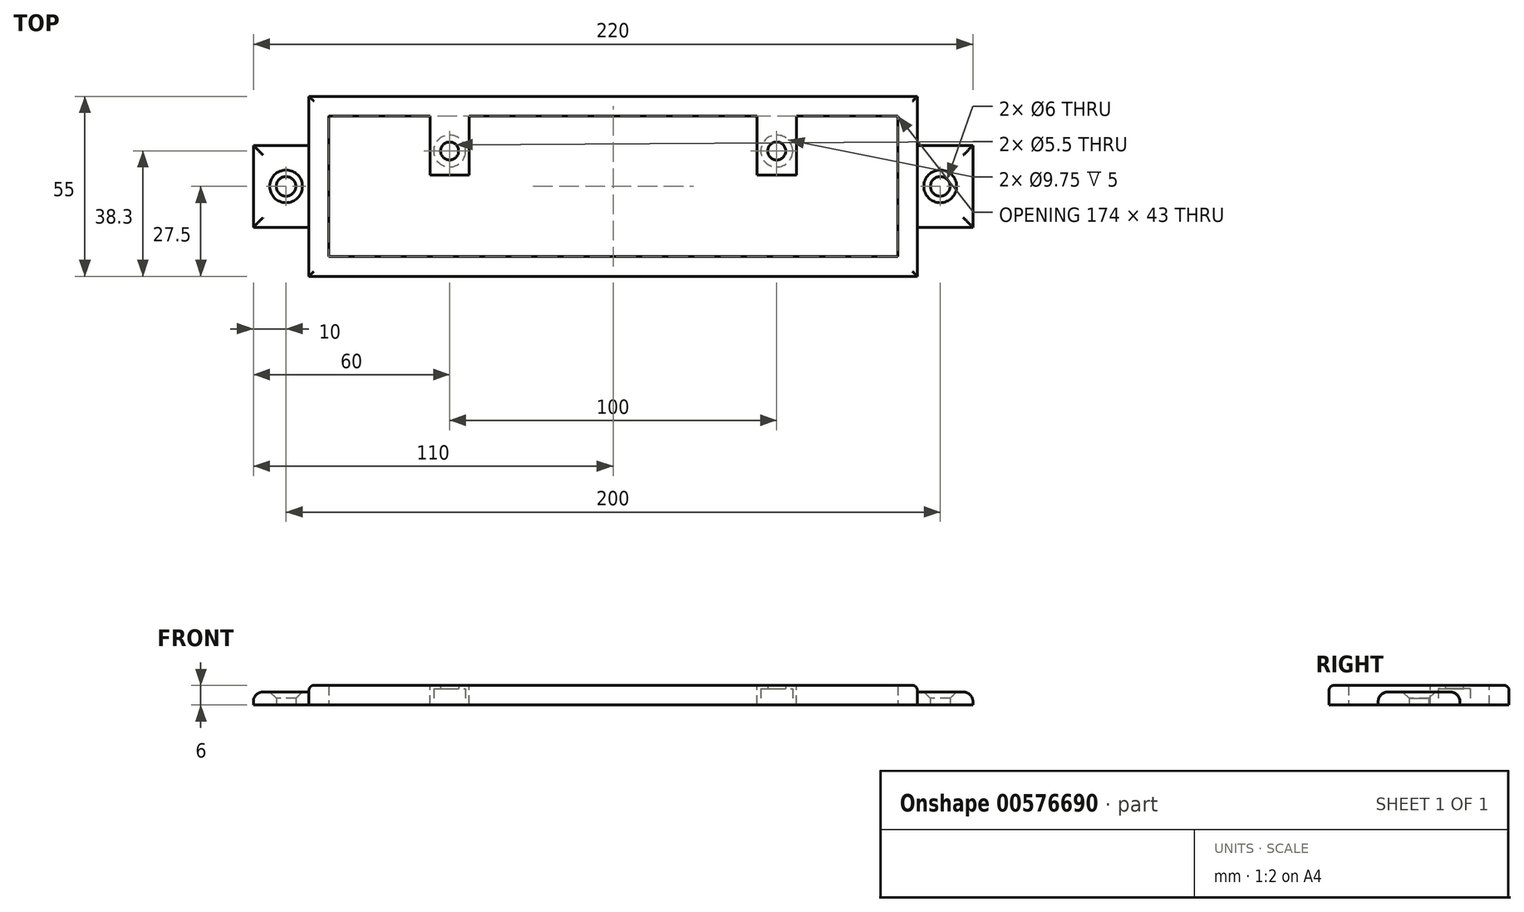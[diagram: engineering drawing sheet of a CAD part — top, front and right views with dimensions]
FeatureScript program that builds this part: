
annotation { "Feature Type Name" : "Feature", "Feature Type Description" : "" }
export const myFeature = defineFeature(function(context is Context, id is Id, definition is map)
    precondition{}
    {
        {
            var Q0;
            Q0=qCreatedBy(makeId("Top.planeOp"),FACE);
            var sketch = newSketch(context, id + "F0", { "sketchPlane" : qUnion([Q0])});
            skLineSegment(sketch, "E0.bottom", {"start": v(110, 12.5) * mm, "end": v(93, 12.5) * mm});
            skLineSegment(sketch, "E0.top", {"start": v(110, -12.5) * mm, "end": v(93, -12.5) * mm});
            skLineSegment(sketch, "E0.left", {"start": v(110, 12.5) * mm, "end": v(110, -12.5) * mm});
            skLineSegment(sketch, "E0.right", {"start": v(-110, 12.5) * mm, "end": v(-110, -12.5) * mm});
            skPoint(sketch, "E0.middle", {"position": v(0, 0) * mm});
            skLineSegment(sketch, "E1.bottom", {"start": v(93, 27.5) * mm, "end": v(-93, 27.5) * mm});
            skLineSegment(sketch, "E1.top", {"start": v(93, -27.5) * mm, "end": v(-93, -27.5) * mm});
            skLineSegment(sketch, "E1.left", {"start": v(93, 27.5) * mm, "end": v(93, -27.5) * mm});
            skLineSegment(sketch, "E1.right", {"start": v(-93, 27.5) * mm, "end": v(-93, -27.5) * mm});
            skLineSegment(sketch, "E2.0", {"start": v(87, 21.5) * mm, "end": v(-87, 21.5) * mm});
            skLineSegment(sketch, "E2.1", {"start": v(87, 21.5) * mm, "end": v(87, -21.5) * mm});
            skLineSegment(sketch, "E2.2", {"start": v(87, -21.5) * mm, "end": v(-87, -21.5) * mm});
            skLineSegment(sketch, "E2.3", {"start": v(-87, 21.5) * mm, "end": v(-87, -21.5) * mm});
            skCircle(sketch, "E3", {"center": v(-100, 0) * mm, "radius": 3 * mm});
            skPoint(sketch, "E4.centerSnap0", {"position": v(93, 0) * mm});
            skLineSegment(sketch, "E5", {"start": v(0, -80.82) * mm, "end": v(0, 84.78) * mm, "construction": true});
            skCircle(sketch, "E6.MirrorC", {"center": v(100, 0) * mm, "radius": 3 * mm});
            skLineSegment(sketch, "E7.bottom", {"start": v(90.5, 25.8) * mm, "end": v(-90.5, 25.8) * mm, "construction": true});
            skLineSegment(sketch, "E7.top", {"start": v(90.5, -25.8) * mm, "end": v(-90.5, -25.8) * mm, "construction": true});
            skLineSegment(sketch, "E7.left", {"start": v(90.5, 25.8) * mm, "end": v(90.5, -25.8) * mm, "construction": true});
            skLineSegment(sketch, "E7.right", {"start": v(-90.5, 25.8) * mm, "end": v(-90.5, -25.8) * mm, "construction": true});
            skLineSegment(sketch, "E8.trimOffspring", {"start": v(-93, 12.5) * mm, "end": v(-110, 12.5) * mm});
            skLineSegment(sketch, "E9.trimOffspring", {"start": v(-93, -12.5) * mm, "end": v(-110, -12.5) * mm});
            skPoint(sketch, "E10", {"position": v(-50, 10.8) * mm});
            skPoint(sketch, "E11.MirrorP", {"position": v(50, 10.8) * mm});
            skSolve(sketch);
        }
        {
            var Q0;
            {var subQ4=sQuery(id+"F0.wireOp",EDGE,"E1.bottom");Q0=makeQuery(id+"F0.imprint","IMPRINT",FACE,{"disambiguationData":[TD([[makeQuery(id+"F0.imprint","IMPRINT",EDGE,{"derivedFrom":subQ4}),1.0]])]});}
            extrude(context, id + "F1", {"entities" : qUnion([Q0]), "depth" : 6 * mm, "offsetDistance" : 25 * mm});
        }
        {
            var Q0;
            Q0 = qSketchRegion(id + "F0", true);
            extrude(context, id + "F2", {"entities" : qUnion([Q0]), "operationType" : NewBodyOperationType.ADD, "depth" : 4 * mm, "offsetDistance" : 25 * mm});
        }
        {
            var Q0;
            Q0=makeQuery(id+"F1.opExtrude","CAP_FACE",FACE,{"disambiguationData":[OSD([sQuery(id+"F0.wireOp",EDGE,"E1.bottom"),sQuery(id+"F0.wireOp",EDGE,"E1.top"),sQuery(id+"F0.wireOp",EDGE,"E1.left"),sQuery(id+"F0.wireOp",EDGE,"E1.right"),sQuery(id+"F0.wireOp",EDGE,"E2.0"),sQuery(id+"F0.wireOp",EDGE,"E2.1"),sQuery(id+"F0.wireOp",EDGE,"E2.2"),sQuery(id+"F0.wireOp",EDGE,"E2.3")])],"isStart":false});
            var sketch = newSketch(context, id + "F3", { "sketchPlane" : qUnion([Q0])});
            skLineSegment(sketch, "E12", {"start": v(0, -57.78) * mm, "end": v(0, 65.6) * mm, "construction": true});
            skLineSegment(sketch, "E13.bottom", {"start": v(-56, 21.5) * mm, "end": v(-44, 21.5) * mm});
            skLineSegment(sketch, "E13.top", {"start": v(-56, 3.5) * mm, "end": v(-44, 3.5) * mm});
            skLineSegment(sketch, "E13.left", {"start": v(-56, 21.5) * mm, "end": v(-56, 3.5) * mm});
            skLineSegment(sketch, "E13.right", {"start": v(-44, 21.5) * mm, "end": v(-44, 3.5) * mm});
            skLineSegment(sketch, "E14.MirrorCS", {"start": v(56, 21.5) * mm, "end": v(56, 3.5) * mm});
            skLineSegment(sketch, "E15.MirrorCS", {"start": v(44, 21.5) * mm, "end": v(44, 3.5) * mm});
            skLineSegment(sketch, "E16.MirrorCS", {"start": v(56, 3.5) * mm, "end": v(44, 3.5) * mm});
            skSolve(sketch);
        }
        {
            var Q0;
            Q0=makeQuery(id+"F3.imprint","IMPRINT",FACE,{"disambiguationData":[TD([[makeQuery(id+"F3.imprint","IMPRINT",EDGE,{"derivedFrom":sQuery(id+"F3.wireOp",EDGE,"E13.bottom")}),1.0]])]});
            var Q1;
            {var subQ0=sQuery(id+"F3.wireOp",EDGE,"E14.MirrorCS");Q1=makeQuery(id+"F3.imprint","IMPRINT",FACE,{"disambiguationData":[TD([[makeQuery(id+"F3.imprint","IMPRINT",EDGE,{"derivedFrom":subQ0}),-1.0]])]});}
            extrude(context, id + "F4", {"entities" : qUnion([Q0, Q1]), "operationType" : NewBodyOperationType.ADD, "oppositeDirection" : true, "depth" : 6 * mm, "offsetDistance" : 25 * mm});
        }
        {
            var Q0;
            Q0=sQuery(id+"F0.wireOp",VERTEX,"E10");
            var Q1;
            Q1=sQuery(id+"F0.wireOp",VERTEX,"E11.MirrorP");
            var Q2;
            Q2=makeQuery(id+"F1.opExtrude","SWEPT_BODY",BODY,{"disambiguationData":[OSD([sQuery(id+"F0.wireOp",EDGE,"E1.bottom"),sQuery(id+"F0.wireOp",EDGE,"E1.top"),sQuery(id+"F0.wireOp",EDGE,"E1.left"),sQuery(id+"F0.wireOp",EDGE,"E1.right"),sQuery(id+"F0.wireOp",EDGE,"E2.0"),sQuery(id+"F0.wireOp",EDGE,"E2.1"),sQuery(id+"F0.wireOp",EDGE,"E2.2"),sQuery(id+"F0.wireOp",EDGE,"E2.3")])]});
            hole(context, id + "F5", {"style" : HoleStyle.C_BORE, "endStyle" : HoleEndStyle.THROUGH, "oppositeDirection" : true, "standardTappedOrClearance" : lookupTablePath({ "standard" : "ISO", "fit" : "Normal", "size" : "M5", "type" : "Clearance" }), "standardBlindInLast" : lookupTablePath({ "fit" : "Standard", "standard" : "ISO", "size" : "M5", "type" : "Clearance" }), "holeDiameter" : 5.5 * mm, "cBoreDiameter" : 9.75 * mm, "cBoreDepth" : 5 * mm, "isTappedThrough" : true, "tappedDepth" : 12 * mm, "tapClearance" : 3, "locations" : qUnion([Q0, Q1]), "scope" : qUnion([Q2])});
        }
        {
            var Q0;
            Q0=makeQuery(id+"F2.opExtrude","CAP_EDGE",EDGE,{"disambiguationData":[OSD([sQuery(id+"F0.wireOp",EDGE,"E6.MirrorC")])],"isStart":false});
            var Q1;
            Q1=makeQuery(id+"F2.opExtrude","CAP_EDGE",EDGE,{"disambiguationData":[OSD([sQuery(id+"F0.wireOp",EDGE,"E3")])],"isStart":false});
            chamfer(context, id + "F6", {"entities" : qUnion([Q0, Q1]), "width" : 2 * mm, "tangentPropagation" : true});
        }
        {
            var Q0;
            Q0=makeQuery(id+"F2.opExtrude","CAP_EDGE",EDGE,{"disambiguationData":[OSD([sQuery(id+"F0.wireOp",EDGE,"E0.right")])],"isStart":false});
            var Q1;
            Q1=makeQuery(id+"F2.opExtrude","CAP_EDGE",EDGE,{"disambiguationData":[OSD([sQuery(id+"F0.wireOp",EDGE,"E8.trimOffspring")])],"isStart":false});
            var Q2;
            Q2=makeQuery(id+"F2.opExtrude","CAP_EDGE",EDGE,{"disambiguationData":[OSD([sQuery(id+"F0.wireOp",EDGE,"E9.trimOffspring")])],"isStart":false});
            var Q3;
            Q3=makeQuery(id+"F2.opExtrude","CAP_EDGE",EDGE,{"disambiguationData":[OSD([sQuery(id+"F0.wireOp",EDGE,"E0.bottom")])],"isStart":false});
            var Q4;
            Q4=makeQuery(id+"F2.opExtrude","CAP_EDGE",EDGE,{"disambiguationData":[OSD([sQuery(id+"F0.wireOp",EDGE,"E0.left")])],"isStart":false});
            var Q5;
            Q5=makeQuery(id+"F2.opExtrude","CAP_EDGE",EDGE,{"disambiguationData":[OSD([sQuery(id+"F0.wireOp",EDGE,"E0.top")])],"isStart":false});
            fillet(context, id + "F7", {"entities" : qUnion([Q0, Q1, Q2, Q3, Q4, Q5]), "radius" : 3 * mm, "tangentPropagation" : true, "allowEdgeOverflow" : false});
        }
        {
            var Q0;
            Q0=makeQuery(id+"F1.opExtrude","CAP_EDGE",EDGE,{"disambiguationData":[OSD([sQuery(id+"F0.wireOp",EDGE,"E1.bottom")])],"isStart":false});
            var Q1;
            Q1=makeQuery(id+"F1.opExtrude","CAP_EDGE",EDGE,{"disambiguationData":[OSD([sQuery(id+"F0.wireOp",EDGE,"E1.right")])],"isStart":false});
            var Q2;
            Q2=makeQuery(id+"F1.opExtrude","CAP_EDGE",EDGE,{"disambiguationData":[OSD([sQuery(id+"F0.wireOp",EDGE,"E1.top")])],"isStart":false});
            var Q3;
            Q3=makeQuery(id+"F1.opExtrude","CAP_EDGE",EDGE,{"disambiguationData":[OSD([sQuery(id+"F0.wireOp",EDGE,"E1.left")])],"isStart":false});
            fillet(context, id + "F8", {"entities" : qUnion([Q0, Q1, Q2, Q3]), "radius" : 1.5 * mm, "tangentPropagation" : true, "allowEdgeOverflow" : false});
        }
    });
